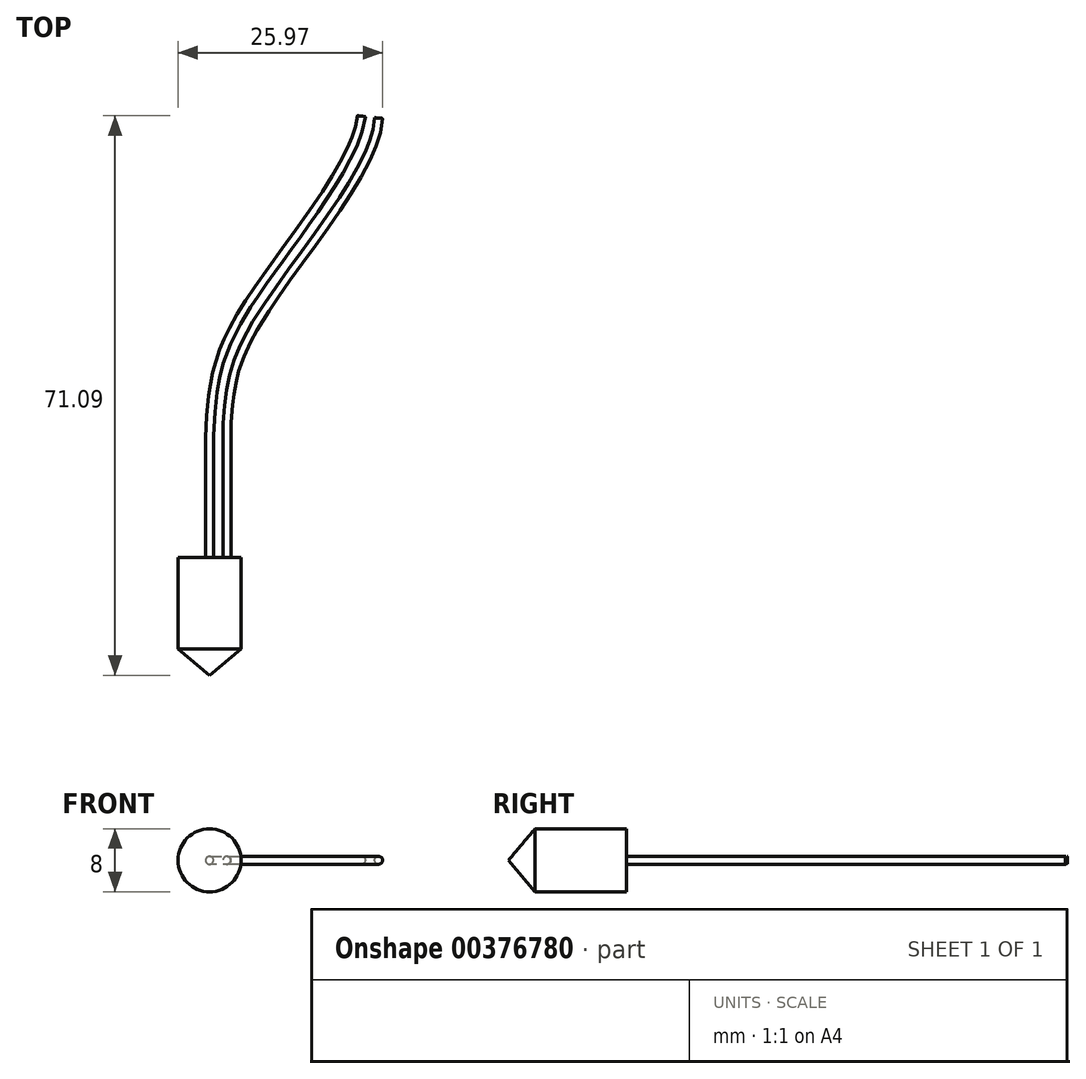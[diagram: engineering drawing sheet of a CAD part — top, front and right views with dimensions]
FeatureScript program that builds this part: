
annotation { "Feature Type Name" : "Feature", "Feature Type Description" : "" }
export const myFeature = defineFeature(function(context is Context, id is Id, definition is map)
    precondition{}
    {
        {
            var Q0;
            Q0=qCreatedBy(makeId("Top.planeOp"),FACE);
            var sketch = newSketch(context, id + "F0", { "sketchPlane" : qUnion([Q0])});
            skLineSegment(sketch, "E0", {"start": v(0, -14.7) * mm, "end": v(4, -11.34) * mm});
            skLineSegment(sketch, "E1", {"start": v(4, -11.34) * mm, "end": v(4, 0.3) * mm});
            skLineSegment(sketch, "E2", {"start": v(4, 0.3) * mm, "end": v(0, 0.3) * mm});
            skLineSegment(sketch, "E3", {"start": v(0, 0.3) * mm, "end": v(0, -14.7) * mm});
            skLineSegment(sketch, "E4", {"start": v(0, 0.3) * mm, "end": v(0, 12.74) * mm});
            skFitSpline(sketch, "E5", {"points": [v(0, 12.74) * mm, v(4.52, 31.88) * mm, v(19.29, 56.34) * mm], "startDerivative": vector(0.05, 58.87) * mm, "endDerivative": vector(3.98, 35.62) * mm});
            skFitSpline(sketch, "E6.0", {"points": [v(2.2, 12.74) * mm, v(2.2, 15.16) * mm, v(2.28, 18.2) * mm, v(2.66, 21.49) * mm, v(3.12, 23.68) * mm, v(3.78, 25.73) * mm, v(4.54, 27.47) * mm, v(5.32, 28.93) * mm, v(5.99, 30.09) * mm, v(6.75, 31.3) * mm, v(7.9, 33.03) * mm, v(9.53, 35.34) * mm, v(11.66, 38.27) * mm, v(13.86, 41.3) * mm, v(16, 44.36) * mm, v(17.96, 47.4) * mm, v(19.63, 50.37) * mm, v(20.89, 53.25) * mm, v(21.37, 55.14) * mm, v(21.47, 56.1) * mm]});
            skLineSegment(sketch, "E6.1", {"start": v(2.2, 0.3) * mm, "end": v(2.2, 12.74) * mm});
            skLineSegment(sketch, "E7", {"start": v(19.29, 56.34) * mm, "end": v(17.44, 46.62) * mm});
            skSolve(sketch);
        }
        {
            var Q0;
            Q0=makeQuery(id+"F0.imprint","IMPRINT",FACE,{"disambiguationData":[TD([[makeQuery(id+"F0.imprint","IMPRINT",EDGE,{"derivedFrom":sQuery(id+"F0.wireOp",EDGE,"E0")}),1.0]])]});
            var Q1;
            Q1=sQuery(id+"F0.wireOp",EDGE,"E3");
            revolve(context, id + "F1", {"entities" : qUnion([Q0]), "axis" : qUnion([Q1]), "revolveType" : RevolveType.FULL});
        }
        {
            var Q0;
            Q0=makeQuery(id+"F1.opRevolve","SWEPT_FACE",FACE,{"disambiguationData":[OSD([sQuery(id+"F0.wireOp",EDGE,"E2")])]});
            var sketch = newSketch(context, id + "F2", { "sketchPlane" : qUnion([Q0])});
            skCircle(sketch, "E8", {"center": v(0, 0) * mm, "radius": 0.5 * mm});
            skCircle(sketch, "E9", {"center": v(-2.2, 0) * mm, "radius": 0.5 * mm});
            skSolve(sketch);
        }
        {
            var Q0;
            Q0=makeQuery(id+"F2.imprint","IMPRINT",FACE,{"disambiguationData":[TD([[makeQuery(id+"F2.imprint","IMPRINT",EDGE,{"derivedFrom":sQuery(id+"F2.wireOp",EDGE,"E8")}),1.0]])]});
            var Q1;
            Q1=sQuery(id+"F0.wireOp",EDGE,"E4");
            var Q2;
            Q2=sQuery(id+"F0.wireOp",EDGE,"E5");
            sweep(context, id + "F3", {"profiles" : qUnion([Q0]), "path" : qUnion([Q1, Q2])});
        }
        {
            var Q0;
            Q0=makeQuery(id+"F2.imprint","IMPRINT",FACE,{"disambiguationData":[TD([[makeQuery(id+"F2.imprint","IMPRINT",EDGE,{"derivedFrom":sQuery(id+"F2.wireOp",EDGE,"E9")}),1.0]])]});
            var Q1;
            Q1=sQuery(id+"F0.wireOp",EDGE,"E6.1");
            var Q2;
            Q2=sQuery(id+"F0.wireOp",EDGE,"E6.0");
            sweep(context, id + "F4", {"profiles" : qUnion([Q0]), "path" : qUnion([Q1, Q2])});
        }
    });
